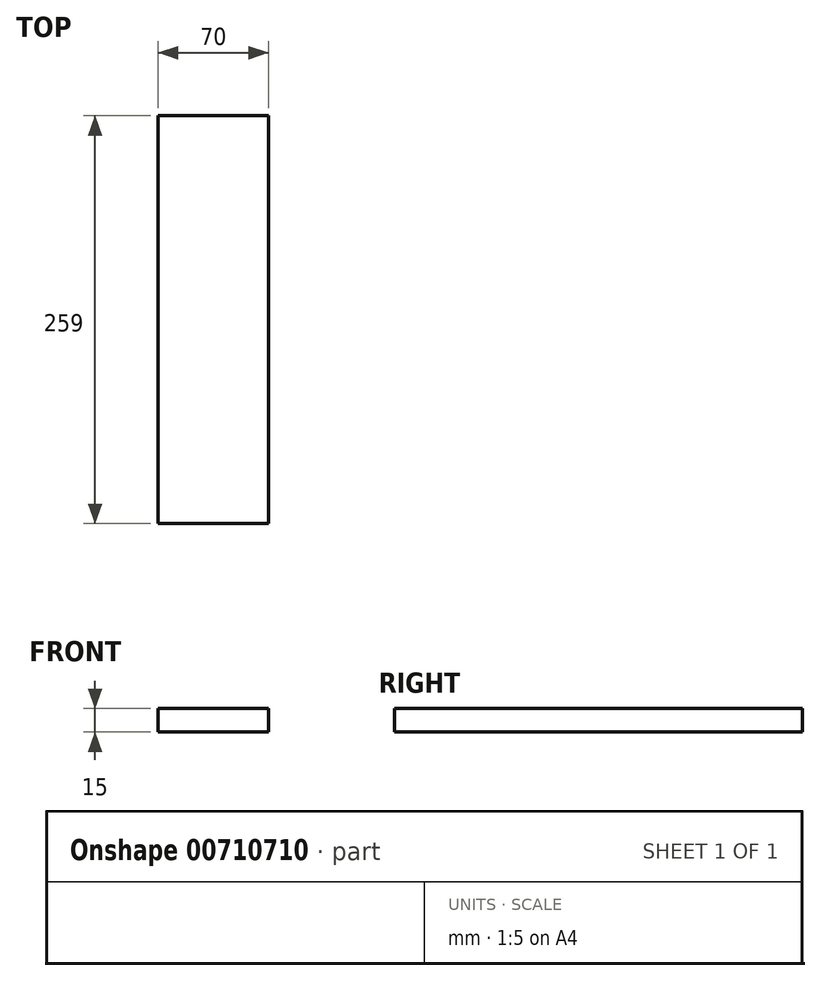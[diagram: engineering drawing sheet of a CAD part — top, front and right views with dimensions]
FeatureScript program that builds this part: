
annotation { "Feature Type Name" : "Feature", "Feature Type Description" : "" }
export const myFeature = defineFeature(function(context is Context, id is Id, definition is map)
    precondition{}
    {
        {
            assignVariable(context, id + "F0", {"name" : "l", "anyValue" : 259});
        }
        {
            var Q0;
            Q0=qCreatedBy(makeId("Front.planeOp"),FACE);
            var sketch = newSketch(context, id + "F1", { "sketchPlane" : qUnion([Q0])});
            skLineSegment(sketch, "E0.bottom", {"start": v(0, 0) * mm, "end": v(70, 0) * mm});
            skLineSegment(sketch, "E0.top", {"start": v(0, 15) * mm, "end": v(70, 15) * mm});
            skLineSegment(sketch, "E0.left", {"start": v(0, 0) * mm, "end": v(0, 15) * mm});
            skLineSegment(sketch, "E0.right", {"start": v(70, 0) * mm, "end": v(70, 15) * mm});
            skSolve(sketch);
        }
        {
            var Q0;
            Q0 = qSketchRegion(id + "F1", true);
            extrude(context, id + "F2", {"entities" : qUnion([Q0]), "depth" : (getVariable(context, 'l')) * mm, "offsetDistance" : 25 * mm});
        }
    });
